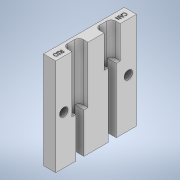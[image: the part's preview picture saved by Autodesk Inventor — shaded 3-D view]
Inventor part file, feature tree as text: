
AUTODESK INVENTOR PART (.ipt)
format: ipt  version: 2021 (Build 250183000, 183)  size: 310,272 bytes
history: native  units: in
note: dims shown in document units (in); Inventor stores cm internally (conversion verified against a paired STEP export)
features: sketch x5, extrude x4, fillet x1, hole x1
ambient origin geometry x8: Origin, YZ Plane, XZ Plane, XY Plane, X Axis, Y Axis, Z Axis, Center Point
bodies: Solid1 (feature_tree)
feature tree (11):
  extrude  "Extrusion1"  Depth=3.0in
  extrude  "Extrusion2"  Depth=0.5in
  fillet  "Fillet1"  Radius=1.75in
  hole  "Hole1"  [1 undecoded]
  extrude  "Extrusion3"  Depth=0.25in
  extrude  "Extrusion4"  Depth=0.1875in
  sketch  "Sketch1"  dims[d0=2.5in d1=3.0in]
  sketch  "Sketch2"  dims[d2=0.375in d3=0.0in d4=0.5in d5=1.75in d6=0.5in]
  sketch  "Sketch3"  dims[d7=1.0in d8=0.5in]
  sketch  "Sketch4"  dims[d9=0.5in d10=0.25in]
  sketch  "Sketch5"  dims[d11=0.25in d12=1.75in d13=0.28in d14=0.0in d15=0.14in d16=0.2656in d17=0.5in d18=0.375in d19=0.25in d20=0.5635in d21=1.0in d22=0.8108in d23=1.5in d24=0.25in d26=1.5in d27=0.25in d28=0.05in d29=0.0in d34=0.47in d35=0.47in d36=0.25in d37=0.1875in d38=0.0in]
note: 1 required parameter value undecoded (feature->parameter linkage not recoverable at this tier; creation-order binding heuristic only, values carry confidence <= 0.55)
